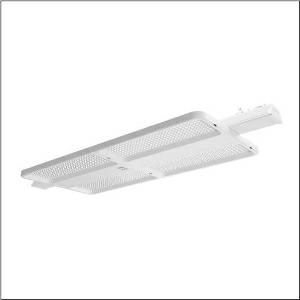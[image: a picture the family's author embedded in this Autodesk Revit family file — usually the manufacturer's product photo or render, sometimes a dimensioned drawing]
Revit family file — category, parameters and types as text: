
# Revit family: highbay_21_fur_licross_r__tragschiene_maxi_52hn12db4qla01_0232
name_source: partatom
category: Lighting Fixtures
units: mm (PartAtom-declared; Revit-internal decimal feet)

## family parameters
Cut with Voids When Loaded = No
Host = Face
Light Source = No
Part Type = Normal
Room Calculation Point = No
Round Connector Dimension = Use Diameter
Shared = No

## types (1)
- --- (1 x LED, 38000 lm, 198.2 W, 4000K)
    Apparent Load = 198 VA
    CIE Flux Codes = 90 98 100 100 100
    Color Rendering = 80
    Color Temperature = 4000K
    Default Elevation = 1800 mm
    Description = high bay luminaire Highbay 21 for Licross® trunking rail maxi; direct symmetric wide distribution, light control with lens of PMMA; UGR ≤ 22 (X = 4H | Y = 8H | S = 0.25H | reflection values 70/50/20); luminous flux: 38.000lm; light colour: 840, colour temperature: 4000K, MacAdam ≤ 3 SDCM (initial), colour rendering: CRI > 80; luminous efficacy: 191,7lm/W; rated service life: 75.000h (L80/B50) at AT= ta max; control: Bluetooth® Mesh; for wireless networking: Node multi-sensor luminaire for setting up a local control solution without a higher-level application controller, intelligence completely integrated into the luminaire; with auto-swarm function: leading lighting creates safety. The function is already active without any „out-of-the-box“ commissioning; commissioning is not necessary thanks to „out-of-the-box“ functions: basic functions (presence lighting, follow-up times, fading times, etc.) are already preset at the factory; no control line such as DALI between the Node multi-sensor luminaires and Nodes is required, wireless integration of other Node luminaires and Node multi-sensor luminaires into the network is possible; number of Node multi-sensor luminaires in the project can be expanded as required, network sizes > 300 Nodes can be realized; can also be connected to lighting or building automation via various gateways upon request; integrated DALI2 ECG provides luminaire data (according to IEC62386, Part 251), energy data (Part 252), and monitoring and analytics data (Part 253) to higher-level systems for further processing; luminaire with PIR sensor (passive-infrared); with light sensor; luminaire connection: plug, 5-pole, with phase selectionmains connection: 230..240V, AC 50/60Hz; connected load: 198,2W; protection rating (complete): IP64; insulation class (complete): insulation class I (protective earthing); protection symbol: D; certification: CE, ENEC, VDE, UKCA; internal wiring halogen-free; luminaire corresponds to IFS (International Featured Standards) requirements for safety and quality in the food industry; LABS conformity tested according to VDMA 24364:2018-05; housing frame of high-performance plastic PA6, matt traffic white (RAL 9016); cover of PMMA; fixing on rail side of steel, galvanised, white; blank cover of PC/ABS, traffic white (RAL 9016); dimension (LxWxH): 1.250 x 442 x 71mm; permissible operating ambient temperature: -20..+40°C (reducing of maximum allowable ambient temperature of 5°C with ceiling mounting); packaging unit: 1 piece
    Height = 72 mm  [stored 0.23622 ft]
    Lamp = 1 x LED
    Lamp Light Flux = 38000 lm
    Lamp Power = 198.2 W
    Lamp count = 1
    Length = 946 mm
    Luminous efficacy = 192 lm/W
    Manufacturer = Siteco
    ModVariant = No
    Model = 52HN12DB4QLA01
    Mounting Place = Ceiling
    Mounting Type = Pendant
    Number of Poles = 1
    OnlyDefault = Yes
    Power Factor = 1
    Product Name = Highbay 21 für Licross® Tragschiene maxi
    Product group = high bay luminaire
    ProductGroupID = 901
    Protection Class = Protection class I
    Protection Degree = IP 64
    RLX_Detail_Level = 1
    RLX_Emergency_Light_Flux = 0 lm
    RLX_Emergency_Type = 0
    RLX_Emergency_Type_DB = No
    RlxData = <blob elided: 131341 chars, md5=bad06ba8>
    Socket = socket
    Standby Power = 0 W
    System Light Flux = 38001 lm
    System Power = 198 W
    Type Comments = factory setting: luminous flux: 100 % | dim-lin: 254 | 918 mA
    Type Image = l_1363271.jpg
    URL = http://relux.com
    VarID = @adj_011283
    Voltage = 0 V
    Weight = 0.00 kg
    Width = 442 mm

note: [stored X ft] marks values corroborated as IEEE doubles in the binary element streams (Revit-internal decimal feet)

## geometry (parser evidence)
native form markers: Blend x4, Sweep x10
no freeform markers — native parametric forms only
